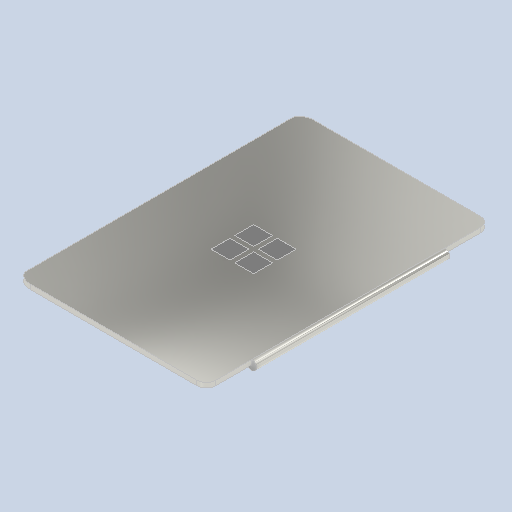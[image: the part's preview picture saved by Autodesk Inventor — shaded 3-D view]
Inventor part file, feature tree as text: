
AUTODESK INVENTOR PART (.ipt)
format: ipt  version: 2022 (Build 260153000, 153)  size: 213,504 bytes
history: native  units: mm
features: extrude x6, sketch x4, plane x1
ambient origin geometry x8: Origin, YZ Plane, XZ Plane, XY Plane, X Axis, Y Axis, Z Axis, Center Point
bodies: Body1 (feature_tree)
feature tree (11):
  plane  "Work Plane1"
  sketch  "Sketch2"  dims[d7=0.5mm d8=0.0mm d9=0.49mm d10=0.0mm]
  extrude  "Extrusion2"  Depth=0.49mm TaperAngle=0.0deg
  extrude  "Extrusion3"  Depth=2.0mm
  extrude  "Extrusion4"  Depth=0.5mm
  extrude  "Extrusion5"  Depth=12.75mm
  extrude  "Extrusion6"  Depth=7.75mm
  extrude  "Extrusion7"  Depth=0.001mm TaperAngle=0.0deg
  sketch  "Sketch3"  dims[d11=2.0mm d12=2.0mm]
  sketch  "Sketch4"  dims[d13=0.5mm d14=0.5mm]
  sketch  "Sketch6"  dims[d15=0.5mm d16=12.75mm d17=7.75mm d18=0.001mm d19=0.0mm d20=0.25mm d21=0.315mm d22=15.0mm d23=0.001mm d24=0.0mm d26=0.0mm d32=21.5mm d33=0.0mm d34=20.425mm d35=0.0mm d36=0.5mm]
